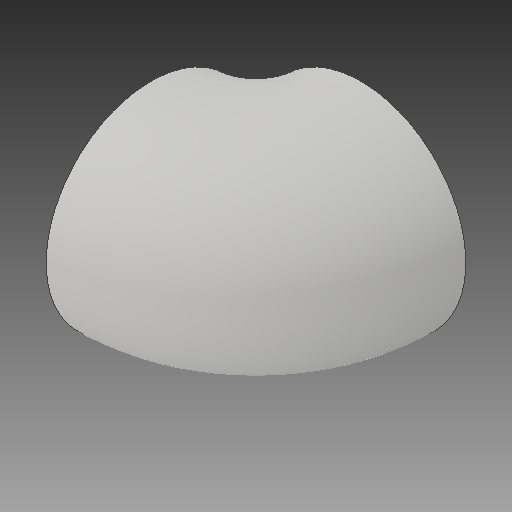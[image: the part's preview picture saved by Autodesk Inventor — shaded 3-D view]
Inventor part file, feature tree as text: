
AUTODESK INVENTOR PART (.ipt)
format: ipt  version: 2017 (Build 210142000, 142)  size: 226,304 bytes
history: native  units: in
note: dims shown in document units (in); Inventor stores cm internally (conversion verified against a paired STEP export)
features: other x2, sketch x2
ambient origin geometry x8: Origin, YZ Plane, XZ Plane, XY Plane, X Axis, Y Axis, Z Axis, Center Point
bodies: Solid1 (feature_tree), Solid2 (feature_tree)
feature tree (4):
  other  "corridor"
  other  "light"
  sketch  "Sketch1"  dims[d1=4.0in]
  sketch  "Sketch4"  dims[d2=90.0deg d11=1.0in d16=0.5833in d17=0.0625in d18=0.0625in d19=0.125in d20=0.25in d21=0.125in d22=45.0deg d23=0.0892in d24=0.0884in d25=90.0deg]
